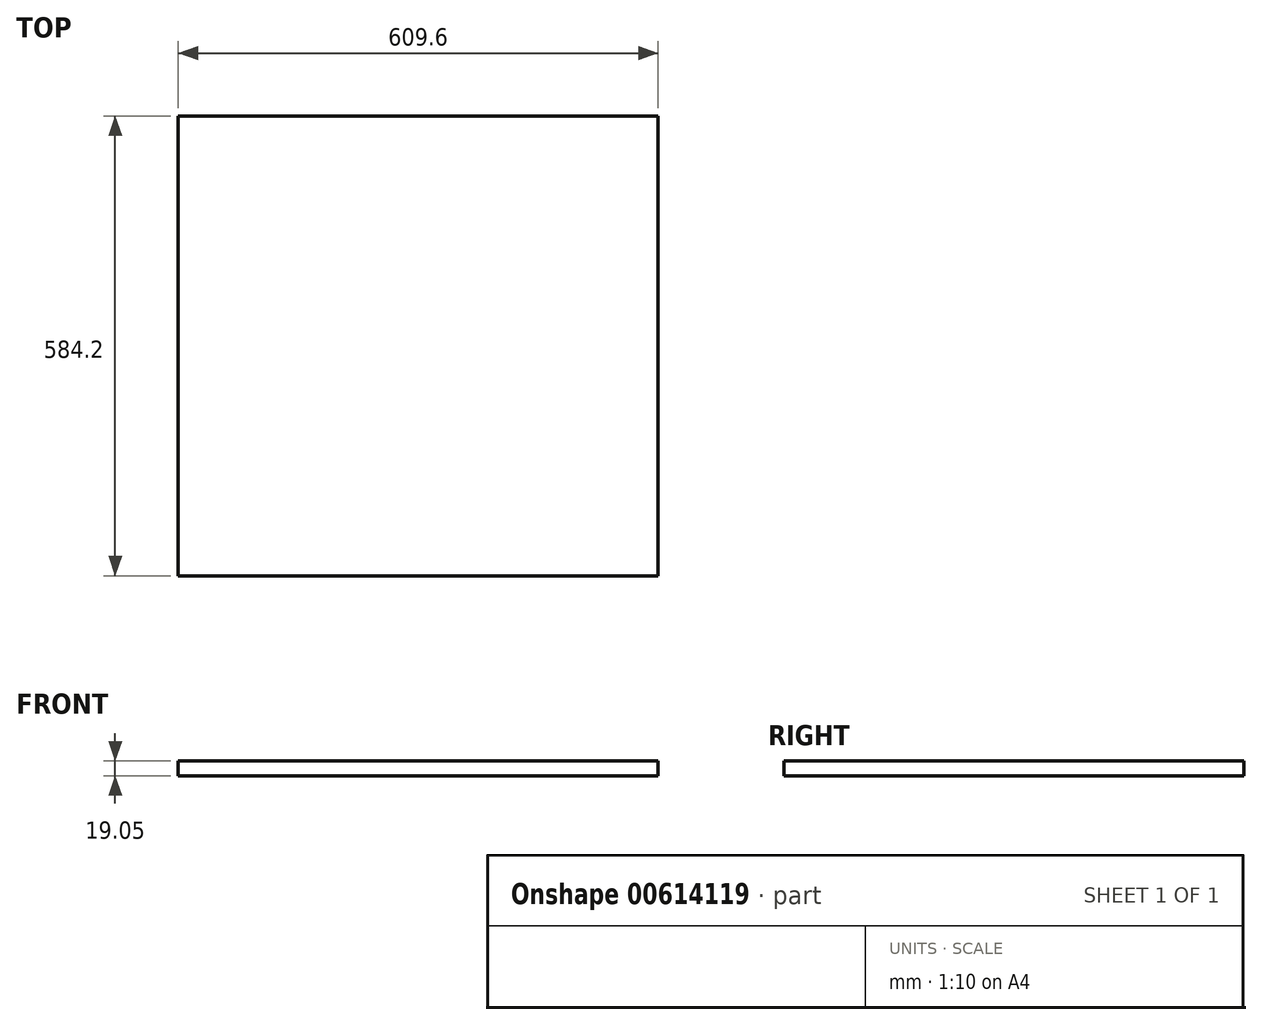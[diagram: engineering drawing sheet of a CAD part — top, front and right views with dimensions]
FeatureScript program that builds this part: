
annotation { "Feature Type Name" : "Feature", "Feature Type Description" : "" }
export const myFeature = defineFeature(function(context is Context, id is Id, definition is map)
    precondition{}
    {
        {
            var Q0;
            Q0=qCreatedBy(makeId("Top.planeOp"),FACE);
            var sketch = newSketch(context, id + "F0", { "sketchPlane" : qUnion([Q0])});
            skLineSegment(sketch, "E0.bottom", {"start": v(304.8, 292.1) * mm, "end": v(-304.8, 292.1) * mm});
            skLineSegment(sketch, "E0.top", {"start": v(304.8, -292.1) * mm, "end": v(-304.8, -292.1) * mm});
            skLineSegment(sketch, "E0.left", {"start": v(304.8, 292.1) * mm, "end": v(304.8, -292.1) * mm});
            skLineSegment(sketch, "E0.right", {"start": v(-304.8, 292.1) * mm, "end": v(-304.8, -292.1) * mm});
            skPoint(sketch, "E0.middle", {"position": v(0, 0) * mm});
            skSolve(sketch);
        }
        {
            var Q0;
            Q0=makeQuery(id+"F0.imprint","IMPRINT",FACE,{"disambiguationData":[TD([[makeQuery(id+"F0.imprint","IMPRINT",EDGE,{"derivedFrom":sQuery(id+"F0.wireOp",EDGE,"E0.bottom")}),1.0]])]});
            extrude(context, id + "F1", {"entities" : qUnion([Q0]), "depth" : 19.05 * mm, "offsetDistance" : 25.4 * mm});
        }
    });
